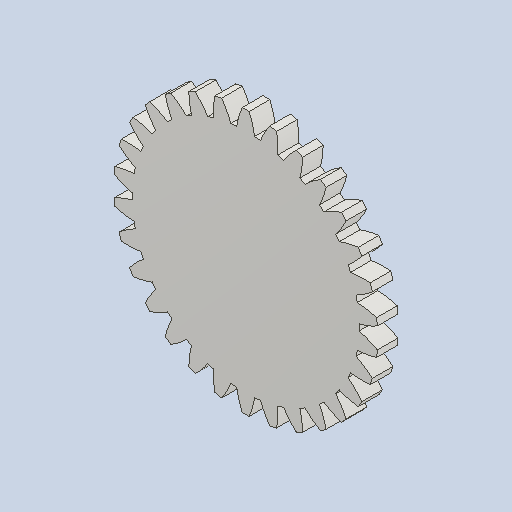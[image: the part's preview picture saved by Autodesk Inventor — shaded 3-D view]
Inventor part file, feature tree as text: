
AUTODESK INVENTOR PART (.ipt)
format: ipt  version: 2023 (Build 270158000, 158)  size: 240,128 bytes
history: native  units: mm (DEFAULTED — no unit token found)
features: plane x3, other x3, sketch x2, extrude x1
ambient origin geometry x8: Origin, YZ Plane, XZ Plane, XY Plane, X Axis, Y Axis, Z Axis, Center Point
bodies: Solid1 (feature_tree)
feature tree (9):
  extrude  "Extrusion1"  Depth=5.0mm TaperAngle=0.0deg
  plane  "Work Plane2"
  plane  "Work Plane8"
  plane  "Work Plane9"
  other  "Spur Gear"
  sketch  "Sketch1"  dims[d0=64.0mm d1=5.0mm d2=0.0mm]
  sketch  "Sketch2"  dims[d3=60.0mm d4=10.0mm d5=0.0mm d16=45.0mm d17=0.0mm d34=1.047198mm d39=0.0mm d41=0.0mm d43=45.0mm d46=45.0mm d47=0.0mm d48=0.0mm]
  other  "Srf1"
  other  "Pitch Diameter"
